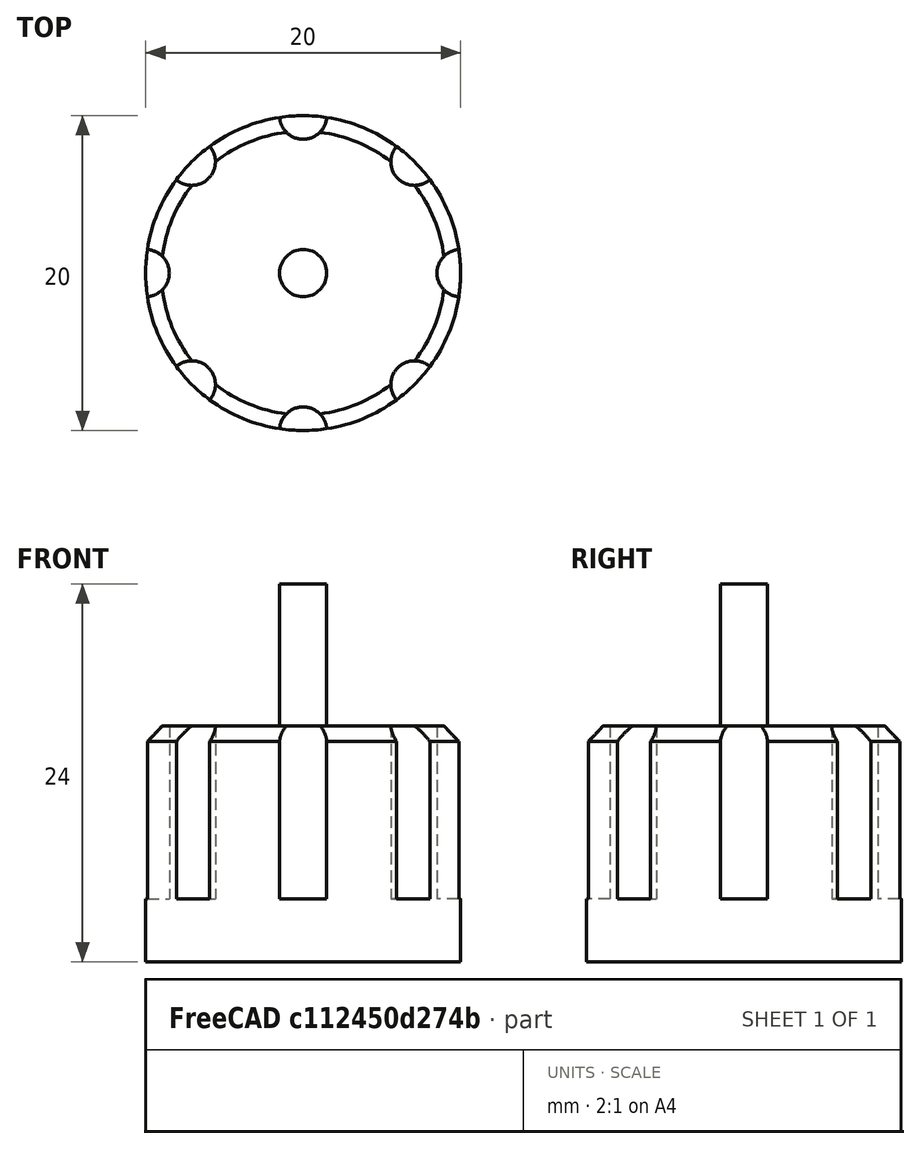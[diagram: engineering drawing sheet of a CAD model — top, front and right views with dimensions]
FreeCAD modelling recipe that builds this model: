
FCSTD DOCUMENT  (FreeCAD 1.0R39319 (Git))
Label: ojt1_t12r01_buttom_potenciometer
License: All rights reserved
LicenseURL: https://en.wikipedia.org/wiki/All_rights_reserved
objects: Part::Cylinder×2, Part::FeaturePython×1, Part::Cut×1, Part::Chamfer×1
note: 4 computed .brp shape members not serialized (recipe doc carries the construction recipe); baked Part::Feature solids carry a one-line shape summary decoded from their .brp

FEATURE [Part::Cylinder] Cylinder  label="Cilindre"
  Angle = 360
  AttacherType = Attacher::AttachEngine3D
  FirstAngle = 0
  Height = 15
  Radius = 10
  SecondAngle = 0
FEATURE [Part::Cylinder] Cylinder001  label="Cilindre001"
  Angle = 360
  AttacherType = Attacher::AttachEngine3D
  FirstAngle = 0
  Height = 20
  Placement = pos=(0,0,4) rot=(0,0,1;0rad)
  Radius = 1.5
  SecondAngle = 0
FEATURE [Part::FeaturePython] Array  # Draft array (typed FeaturePython)
  AlwaysSyncPlacement = false
  Angle = 360
  ArrayType = 1
  Axis = (0,0,1)
  Base = -> Cylinder001
  Center = (10,0,0)
  Count = 8
  ExpandArray = false
  Fuse = false
  IntervalAxis = (0,0,0)
  IntervalX = (100,0,0)
  IntervalY = (0,100,0)
  IntervalZ = (0,0,100)
  NumberCircles = 3
  NumberPolar = 8
  NumberX = 2
  NumberY = 2
  NumberZ = 1
  Placement = pos=(-10,0,0) rot=(0,0,1;0rad)
  PlacementList = 8 placements: [(0,0,4),(2.92893,-7.07107,4),(10,-10,4),(17.0711,-7.07107,4),(20,-1.22465e-15,4),(17.0711,7.07107,4),(10,10,4),(2.92893,7.07107,4)]
  RadialDistance = 50
  ScaleList = (8) [(1,1,1),(1,1,1),(1,1,1),(1,1,1),(1,1,1),(1,1,1),(1,1,1),(1,1,1)]
  Symmetry = 1
  TangentialDistance = 25
FEATURE [Part::Cut] Cut
  Base = -> Cylinder
  Refine = true
  Tool = -> Array
FEATURE [Part::Chamfer] Chamfer
  Base = -> Cut
  EdgeLinks = -> Cut [Edge5,Edge9,Edge13,Edge17,Edge21,Edge25,Edge29,Edge33]
  Edges = 8 edges r=1: [Edge5,Edge9,Edge13,Edge17,Edge21,Edge25,Edge29,Edge33]
